FCSTD DOCUMENT  (FreeCAD 0.19R24267 +99 (Git))
Label: OTP20_Assembly
License: Creative Commons Attribution-NonCommercial-ShareAlike
LicenseURL: http://creativecommons.org/licenses/by-nc-sa/4.0/
objects: App::Link×6, App::DocumentObjectGroup×2, PartDesign::CoordinateSystem×1, App::FeaturePython×1, App::Part×1
note: 1 computed .brp shape members not serialized (recipe doc carries the construction recipe); baked Part::Feature solids carry a one-line shape summary decoded from their .brp
EXTERNAL_REF file=10_Case/OTP20_Case_Assembly.FCStd obj=LCS_Origin
EXTERNAL_REF file=10_Case/OTP20_Case_Assembly.FCStd obj=Model
EXTERNAL_REF file=30_PCB/OTP20_PCB_Assembly.FCStd obj=LCS_Origin
EXTERNAL_REF file=30_PCB/OTP20_PCB_Assembly.FCStd obj=Model
EXTERNAL_REF file=20_COTS/Battery_Pouch.FCStd obj=LCS_0
EXTERNAL_REF file=20_COTS/Battery_Pouch.FCStd obj=Battery_A5

FEATURE [App::DocumentObjectGroup] Parts
FEATURE [PartDesign::CoordinateSystem] LCS_Origin
  AttacherType = Attacher::AttachEngine3D
  MapMode = 2
  Support = -> [X_Axis]
FEATURE [App::DocumentObjectGroup] Constraints
FEATURE [App::FeaturePython] Variables  # WARN: FeaturePython — macro-defined, semantics opaque (R4)
FEATURE [App::Link] OTP20_Case_Assembly
  AssemblyType = Asm4EE
  AttachedBy = #LCS_Origin
  AttachedTo = Parent Assembly#LCS_Origin
  LinkedObject = -> <external 10_Case/OTP20_Case_Assembly.FCStd>#Model
  expr: Placement = LCS_Origin.Placement * AttachmentOffset * OTP20_Case_Assembly#LCS_Origin.Placement ^ -1
FEATURE [App::Link] OTP20_PCB_Assembly
  AssemblyType = Asm4EE
  AttachedBy = #LCS_Origin
  AttachedTo = Parent Assembly#LCS_Origin
  AttachmentOffset = pos=(-50,3,-1.6) rot=(0,0,1;0rad)
  LinkPlacement = pos=(-50,3,-1.6) rot=(0,0,1;0rad)
  LinkedObject = -> <external 30_PCB/OTP20_PCB_Assembly.FCStd>#Model
  Placement = pos=(-50,3,-1.6) rot=(0,0,1;0rad)
  expr: Placement = LCS_Origin.Placement * AttachmentOffset * OTP20_PCB_Assembly#LCS_Origin.Placement ^ -1
FEATURE [App::Link] Battery_Pouch_Cell_Galaxy_S6
  AttachedBy = #LCS_0
  AttachedTo = Parent Assembly#LCS_Origin
  AttachmentOffset = pos=(0,80,-8) rot=(0,0,1;0rad)
  LinkPlacement = pos=(0,80,-8) rot=(0,0,1;0rad)
  LinkedObject = -> <external 20_COTS/Battery_Pouch.FCStd>#Battery_A5
  Placement = pos=(0,80,-8) rot=(0,0,1;0rad)
  SolverId = Placement::ExpressionEngine
  expr: Placement = LCS_Origin.Placement * AttachmentOffset * Battery_Pouch#LCS_0.Placement ^ -1
FEATURE [App::Link] Battery_Pouch_Cell_Galaxy_S6001
  AttachedBy = #LCS_0
  AttachedTo = Battery_Pouch_Cell_Galaxy_S6#LCS_0
  AttachmentOffset = pos=(0,0,4) rot=(0,0,1;0rad)
  LinkPlacement = pos=(0,80,-4) rot=(0,0,1;0rad)
  LinkedObject = -> <external 20_COTS/Battery_Pouch.FCStd>#Battery_A5
  Placement = pos=(0,80,-4) rot=(0,0,1;0rad)
  SolverId = Placement::ExpressionEngine
  expr: Placement = Battery_Pouch_Cell_Galaxy_S6.Placement * Battery_Pouch#LCS_0.Placement * AttachmentOffset * Battery_Pouch#LCS_0.Placement ^ -1
FEATURE [App::Link] Battery_Pouch_Cell_Galaxy_S6002
  AttachedBy = #LCS_0
  AttachedTo = Battery_Pouch_Cell_Galaxy_S6001#LCS_0
  AttachmentOffset = pos=(0,0,4) rot=(0,0,1;0rad)
  LinkPlacement = pos=(0,80,0) rot=(0,0,1;0rad)
  LinkedObject = -> <external 20_COTS/Battery_Pouch.FCStd>#Battery_A5
  Placement = pos=(0,80,0) rot=(0,0,1;0rad)
  SolverId = Placement::ExpressionEngine
  expr: Placement = Battery_Pouch_Cell_Galaxy_S6001.Placement * Battery_Pouch#LCS_0.Placement * AttachmentOffset * Battery_Pouch#LCS_0.Placement ^ -1
FEATURE [App::Link] Battery_Pouch_Cell_Galaxy_S6003
  AttachedBy = #LCS_0
  AttachedTo = Battery_Pouch_Cell_Galaxy_S6002#LCS_0
  AttachmentOffset = pos=(0,0,4) rot=(0,0,1;0rad)
  LinkPlacement = pos=(0,80,4) rot=(0,0,1;0rad)
  LinkedObject = -> <external 20_COTS/Battery_Pouch.FCStd>#Battery_A5
  Placement = pos=(0,80,4) rot=(0,0,1;0rad)
  SolverId = Placement::ExpressionEngine
  expr: Placement = Battery_Pouch_Cell_Galaxy_S6002.Placement * Battery_Pouch#LCS_0.Placement * AttachmentOffset * Battery_Pouch#LCS_0.Placement ^ -1
FEATURE [App::Part] Model
  Configuration = 0
  Group = -> [LCS_Origin,Constraints,Variables,OTP20_Case_Assembly,OTP20_PCB_Assembly,Battery_Pouch_Cell_Galaxy_S6,Battery_Pouch_Cell_Galaxy_S6001,Battery_Pouch_Cell_Galaxy_S6002,Battery_Pouch_Cell_Galaxy_S6003]
  Origin = -> Origin
  Type = Assembly4 Model

RESOLVED EXTERNAL PARTS (link-assembly join: the EXTERNAL_REF files above that resolve inside this repo's crawl, each included once):
---- part 10_Case/OTP20_Case_Assembly.FCStd = doc fcstd_d594046b169b ----
FCSTD DOCUMENT  (FreeCAD 0.19R24267 +99 (Git))
Label: OTP20_Case_Assembly
License: Creative Commons Attribution-NonCommercial-ShareAlike
LicenseURL: http://creativecommons.org/licenses/by-nc-sa/4.0/
objects: Part::FeaturePython×8, App::Link×6, App::DocumentObjectGroup×3, PartDesign::CoordinateSystem×1, App::FeaturePython×1, App::Part×1
note: 9 computed .brp shape members not serialized (recipe doc carries the construction recipe); baked Part::Feature solids carry a one-line shape summary decoded from their .brp
EXTERNAL_REF file=KOH_Plate_Front.FCStd obj=LCS_0
EXTERNAL_REF file=KOH_Plate_Front.FCStd obj=Plate_Front
EXTERNAL_REF file=OTP20_Case_Bezel.FCStd obj=LCS_0
EXTERNAL_REF file=OTP20_Case_Bezel.FCStd obj=Bezel
EXTERNAL_REF file=KOH-2100.FCStd obj=LCS_KOH2100_CornerBottom
EXTERNAL_REF file=KOH_Plate_Front.FCStd obj=LCS_Plate_Front_CornerBottom
EXTERNAL_REF file=KOH-2100.FCStd obj=KOH_2100
EXTERNAL_REF file=KOH-0100.FCStd obj=LCS_0
EXTERNAL_REF file=KOH-0100.FCStd obj=KOH_0100
EXTERNAL_REF file=KOH_Plate_Back.FCStd obj=LCS_Plate_Back_CornerBottom
EXTERNAL_REF file=KOH_Plate_Back.FCStd obj=Plate_Back
EXTERNAL_REF file=KOH_Plate_Back.FCStd obj=LCS_0
EXTERNAL_REF file=KOH_Plate_Front.FCStd obj=LCS_Plate_Front_DisplayCenter
EXTERNAL_REF file=../20_COTS/Waveshare_OLED_0.91in.FCStd obj=LCS_OLEDDisplay_Center
EXTERNAL_REF file=../20_COTS/Waveshare_OLED_0.91in.FCStd obj=OLED_Display

FEATURE [App::DocumentObjectGroup] Parts
FEATURE [PartDesign::CoordinateSystem] LCS_Origin  label="LCS_Case_Origin"
  AttacherType = Attacher::AttachEngine3D
  MapMode = 2
  Support = -> [X_Axis]
FEATURE [App::DocumentObjectGroup] Constraints
FEATURE [App::FeaturePython] Variables  # WARN: FeaturePython — macro-defined, semantics opaque (R4)
FEATURE [App::Link] KOH_Plate_Front_Plate_Front
  AssemblyType = Asm4EE
  AttachedBy = #LCS_0
  AttachedTo = Parent Assembly#LCS_Origin
  LinkedObject = -> <external KOH_Plate_Front.FCStd>#Plate_Front
  expr: Placement = LCS_Origin.Placement * AttachmentOffset * KOH_Plate_Front#LCS_0.Placement ^ -1
FEATURE [App::Link] OTP20_Case_Bezel_Bezel
  AssemblyType = Asm4EE
  AttachedBy = #LCS_0
  AttachedTo = Parent Assembly#LCS_Origin
  AttachmentOffset = pos=(0,2,0) rot=(0,0,1;0rad)
  LinkPlacement = pos=(0,2,0) rot=(0,0,1;0rad)
  LinkedObject = -> <external OTP20_Case_Bezel.FCStd>#Bezel
  Placement = pos=(0,2,0) rot=(0,0,1;0rad)
  expr: Placement = LCS_Origin.Placement * AttachmentOffset * OTP20_Case_Bezel#LCS_0.Placement ^ -1
FEATURE [App::Link] KOH_2100_KOH_2100
  AssemblyType = Asm4EE
  AttachedBy = #LCS_KOH2100_CornerBottom
  AttachedTo = KOH_Plate_Front_Plate_Front#LCS_Plate_Front_CornerBottom
  AttachmentOffset = pos=(0,3,0) rot=(0,0,1;0rad)
  LinkPlacement = pos=(0,3,-14.35) rot=(0,0,1;0rad)
  LinkedObject = -> <external KOH-2100.FCStd>#KOH_2100
  Placement = pos=(0,3,-14.35) rot=(0,0,1;0rad)
  expr: Placement = KOH_Plate_Front_Plate_Front.Placement * KOH_Plate_Front#LCS_Plate_Front_CornerBottom.Placement * AttachmentOffset * KOH_2100#LCS_KOH2100_CornerBottom.Placement ^ -1
FEATURE [App::Link] KOH_0100_KOH_0100
  AssemblyType = Asm4EE
  AttachedBy = #LCS_0
  AttachedTo = KOH_2100_KOH_2100#LCS_KOH2100_CornerBottom
  AttachmentOffset = pos=(105,100,28.7) rot=(0,0,1;3.14159rad)
  LinkPlacement = pos=(52.5,103,14.35) rot=(0,0,1;3.14159rad)
  LinkedObject = -> <external KOH-0100.FCStd>#KOH_0100
  Placement = pos=(52.5,103,14.35) rot=(0,0,1;3.14159rad)
  SolverId = Placement::ExpressionEngine
  expr: Placement = KOH_2100_KOH_2100.Placement * KOH_2100#LCS_KOH2100_CornerBottom.Placement * AttachmentOffset * KOH_0100#LCS_0.Placement ^ -1
FEATURE [App::Link] KOH_Plate_Back_Plate_Back
  AssemblyType = Asm4EE
  AttachedBy = #LCS_Plate_Back_CornerBottom
  AttachedTo = KOH_Plate_Front_Plate_Front#LCS_Plate_Front_CornerBottom
  AttachmentOffset = pos=(0,105,0) rot=(0,0,1;0rad)
  LinkPlacement = pos=(0,105,1.95e-14) rot=(0,0,-1;3.14159rad)
  LinkedObject = -> <external KOH_Plate_Back.FCStd>#Plate_Back
  Placement = pos=(0,105,1.95e-14) rot=(0,0,-1;3.14159rad)
  SolverId = Placement::ExpressionEngine
  expr: Placement = KOH_Plate_Front_Plate_Front.Placement * KOH_Plate_Front#LCS_Plate_Front_CornerBottom.Placement * AttachmentOffset * KOH_Plate_Back#LCS_Plate_Back_CornerBottom.Placement ^ -1
FEATURE [Part::FeaturePython] Screw  label="M3x8-Screw"  # Fasteners workbench fastener (typed FeaturePython)
  AssemblyType = Asm4EE
  AttachedBy = Origin
  AttachedTo = KOH_Plate_Front_Plate_Front#LCS_0
  AttachmentOffset = pos=(46.5,0,10.85) rot=(0,0.707107,-0.707107;3.14159rad)
  Placement = pos=(46.5,0,10.85) rot=(0,0.707107,-0.707107;3.14159rad)
  diameter = 1
  invert = false
  length = 0
  lengthCustom = 8
  matchOuter = false
  offset = 0
  thread = false
  type = 17
  expr: Placement = KOH_Plate_Front_Plate_Front.Placement * KOH_Plate_Front#LCS_0.Placement * AttachmentOffset
FEATURE [Part::FeaturePython] Screw001  label="M3x8-Screw089"  # Fasteners workbench fastener (typed FeaturePython)
  AssemblyType = Asm4EE
  AttachedBy = Origin
  AttachedTo = KOH_Plate_Front_Plate_Front#LCS_0
  AttachmentOffset = pos=(46.5,0,-10.85) rot=(1,0,0;1.5708rad)
  Placement = pos=(46.5,0,-10.85) rot=(1,0,0;1.5708rad)
  diameter = 1
  invert = false
  length = 0
  lengthCustom = 8
  matchOuter = false
  offset = 0
  thread = false
  type = 17
  expr: Placement = KOH_Plate_Front_Plate_Front.Placement * KOH_Plate_Front#LCS_0.Placement * AttachmentOffset
FEATURE [Part::FeaturePython] Screw002  label="M3x8-Screw090"  # Fasteners workbench fastener (typed FeaturePython)
  AssemblyType = Asm4EE
  AttachedBy = Origin
  AttachedTo = KOH_Plate_Front_Plate_Front#LCS_0
  AttachmentOffset = pos=(-46.5,0,10.85) rot=(-1,0,0;4.71239rad)
  Placement = pos=(-46.5,0,10.85) rot=(1,0,0;1.5708rad)
  diameter = 1
  invert = false
  length = 0
  lengthCustom = 8
  matchOuter = false
  offset = 0
  thread = false
  type = 17
  expr: Placement = KOH_Plate_Front_Plate_Front.Placement * KOH_Plate_Front#LCS_0.Placement * AttachmentOffset
FEATURE [Part::FeaturePython] Screw003  label="M3x8-Screw091"  # Fasteners workbench fastener (typed FeaturePython)
  AssemblyType = Asm4EE
  AttachedBy = Origin
  AttachedTo = KOH_Plate_Front_Plate_Front#LCS_0
  AttachmentOffset = pos=(-46.5,0,-10.85) rot=(-0.57735,-0.57735,0.57735;4.18879rad)
  Placement = pos=(-46.5,0,-10.85) rot=(0.57735,0.57735,-0.57735;2.0944rad)
  diameter = 1
  invert = false
  length = 0
  lengthCustom = 8
  matchOuter = false
  offset = 0
  thread = false
  type = 17
  expr: Placement = KOH_Plate_Front_Plate_Front.Placement * KOH_Plate_Front#LCS_0.Placement * AttachmentOffset
FEATURE [Part::FeaturePython] Screw004  label="M3x8-Screw108"  # Fasteners workbench fastener (typed FeaturePython)
  AssemblyType = Asm4EE
  AttachedBy = Origin
  AttachedTo = KOH_Plate_Back_Plate_Back#LCS_0
  AttachmentOffset = pos=(46.5,0,10.85) rot=(-1,0,0;4.71239rad)
  Placement = pos=(-46.5,105,10.85) rot=(0,0.707107,0.707107;3.14159rad)
  diameter = 1
  invert = false
  length = 0
  lengthCustom = 8
  matchOuter = false
  offset = 0
  thread = false
  type = 17
  expr: Placement = KOH_Plate_Back_Plate_Back.Placement * KOH_Plate_Back#LCS_0.Placement * AttachmentOffset
FEATURE [Part::FeaturePython] Screw005  label="M3x8-Screw109"  # Fasteners workbench fastener (typed FeaturePython)
  AssemblyType = Asm4EE
  AttachedBy = Origin
  AttachedTo = KOH_Plate_Back_Plate_Back#LCS_0
  AttachmentOffset = pos=(46.5,0,-10.85) rot=(1,0,0;1.5708rad)
  Placement = pos=(-46.5,105,-10.85) rot=(0,0.707107,0.707107;3.14159rad)
  diameter = 1
  invert = false
  length = 0
  lengthCustom = 8
  matchOuter = false
  offset = 0
  thread = false
  type = 17
  expr: Placement = KOH_Plate_Back_Plate_Back.Placement * KOH_Plate_Back#LCS_0.Placement * AttachmentOffset
FEATURE [Part::FeaturePython] Screw006  label="M3x8-Screw110"  # Fasteners workbench fastener (typed FeaturePython)
  AssemblyType = Asm4EE
  AttachedBy = Origin
  AttachedTo = KOH_Plate_Back_Plate_Back#LCS_0
  AttachmentOffset = pos=(-46.5,0,10.85) rot=(1,0,0;1.5708rad)
  Placement = pos=(46.5,105,10.85) rot=(0,0.707107,0.707107;3.14159rad)
  diameter = 1
  invert = false
  length = 0
  lengthCustom = 8
  matchOuter = false
  offset = 0
  thread = false
  type = 17
  expr: Placement = KOH_Plate_Back_Plate_Back.Placement * KOH_Plate_Back#LCS_0.Placement * AttachmentOffset
FEATURE [Part::FeaturePython] Screw007  label="M3x8-Screw111"  # Fasteners workbench fastener (typed FeaturePython)
  AssemblyType = Asm4EE
  AttachedBy = Origin
  AttachedTo = KOH_Plate_Back_Plate_Back#LCS_0
  AttachmentOffset = pos=(-46.5,0,-10.85) rot=(-1,0,0;4.71239rad)
  Placement = pos=(46.5,105,-10.85) rot=(0,0.707107,0.707107;3.14159rad)
  diameter = 1
  invert = false
  length = 0
  lengthCustom = 8
  matchOuter = false
  offset = 0
  thread = false
  type = 17
  expr: Placement = KOH_Plate_Back_Plate_Back.Placement * KOH_Plate_Back#LCS_0.Placement * AttachmentOffset
FEATURE [App::DocumentObjectGroup] Group  label="Screws"
  Group = -> [Screw,Screw001,Screw002,Screw003,Screw004,Screw005,Screw006,Screw007]
FEATURE [App::Link] Waveshare_OLED_0_91in_OLED_Display
  AssemblyType = Asm4EE
  AttachedBy = #LCS_OLEDDisplay_Center
  AttachedTo = KOH_Plate_Front_Plate_Front#LCS_Plate_Front_DisplayCenter
  AttachmentOffset = pos=(0,-0.09,-2) rot=(0,0,1;3.14159rad)
  LinkPlacement = pos=(36.19,5.3,9.55) rot=(0,-1,0;3.14159rad)
  LinkedObject = -> <external ../20_COTS/Waveshare_OLED_0.91in.FCStd>#OLED_Display
  Placement = pos=(36.19,5.3,9.55) rot=(0,-1,0;3.14159rad)
  expr: Placement = KOH_Plate_Front_Plate_Front.Placement * KOH_Plate_Front#LCS_Plate_Front_DisplayCenter.Placement * AttachmentOffset * Waveshare_OLED_0_91in#LCS_OLEDDisplay_Center.Placement ^ -1
FEATURE [App::Part] Model
  Configuration = 0
  Group = -> [LCS_Origin,Constraints,Variables,KOH_Plate_Front_Plate_Front,OTP20_Case_Bezel_Bezel,KOH_2100_KOH_2100,KOH_0100_KOH_0100,KOH_Plate_Back_Plate_Back,Group,Screw,Screw001,Screw002,Screw003,Screw004,Screw005,Screw006,Screw007,Waveshare_OLED_0_91in_OLED_Display]
  Origin = -> Origin
  Type = Assembly4 Model
---- part 20_COTS/Battery_Pouch.FCStd = doc fcstd_cdebb19cccf6 ----
FCSTD DOCUMENT  (FreeCAD 0.19R24267 +99 (Git))
Label: Battery_Pouch
License: Creative Commons Attribution-NonCommercial-ShareAlike
LicenseURL: http://creativecommons.org/licenses/by-nc-sa/4.0/
objects: PartDesign::CoordinateSystem×2, Sketcher::SketchObject×1, PartDesign::Pad×1, PartDesign::Fillet×1, PartDesign::Body×1, App::Part×1
note: 8 computed .brp shape members not serialized (recipe doc carries the construction recipe); baked Part::Feature solids carry a one-line shape summary decoded from their .brp

FEATURE [PartDesign::CoordinateSystem] LCS_0  label="LCS_Origin"
  AttacherType = Attacher::AttachEngine3D
  MapMode = 2
  Support = -> [X_Axis]
FEATURE [PartDesign::CoordinateSystem] LCS_0001
  AttacherType = Attacher::AttachEngine3D
  MapMode = 2
  Support = -> [X_Axis001]
FEATURE [Sketcher::SketchObject] Sketch
  FullyConstrained = true
  MapMode = 5
  Placement = pos=(0,0,0) rot=(0.57735,0.57735,0.57735;2.0944rad)
  Support = -> [YZ_Plane001]
  sketch-geometry (4):
    g0: LineSegment StartX=-21.35 StartY=0 StartZ=0 EndX=21.35 EndY=0 EndZ=0
    g1: LineSegment StartX=-21.35 StartY=4 StartZ=0 EndX=21.35 EndY=4 EndZ=0
    g2: LineSegment StartX=21.35 StartY=4 StartZ=0 EndX=21.35 EndY=0 EndZ=0
    g3: LineSegment StartX=-21.35 StartY=4 StartZ=0 EndX=-21.35 EndY=0 EndZ=0
  constraints (11):
    c: Horizontal(g0)
    c: Coincident(g2,g1)
    c: Coincident(g2,g0)
    c: Coincident(g3,g1)
    c: Coincident(g3,g0)
    c: Vertical(g3)
    c: Vertical(g2)
    c: Symmetric(g1,g1,g-2)
    c: Distance(g1) = 42.7
    c: DistanceY(g1) = 4
    c: PointOnObject(g-1,g0)
FEATURE [PartDesign::Pad] Pad
  Direction = (1,1,1)
  Length = 93.4
  Length2 = 100
  Midplane = true
  Placement = pos=(0,0,0) rot=(0.57735,0.57735,0.57735;2.0944rad)
  Profile = -> Sketch
  Refine = true
  Type = 0
FEATURE [PartDesign::Fillet] Fillet
  Base = -> Pad [Edge1,Edge2,Edge5,Edge8]
  BaseFeature = -> Pad
  Placement = pos=(0,0,0) rot=(0.57735,0.57735,0.57735;2.0944rad)
  Radius = 1
  Refine = true
  SupportTransform = false
FEATURE [PartDesign::Body] Main
  Group = -> [LCS_0001,Sketch,Pad,Fillet]
  Origin = -> Origin001
  Tip = -> Fillet
FEATURE [App::Part] Battery_A5  label="Cell_Galaxy_S6"
  Group = -> [LCS_0,Main]
  Origin = -> Origin
---- part 30_PCB/OTP20_PCB_Assembly.FCStd = doc fcstd_e5338bbabf42 ----
FCSTD DOCUMENT  (FreeCAD 0.19R24267 +99 (Git))
Label: OTP20_PCB_Assembly
License: Creative Commons Attribution-NonCommercial-ShareAlike
LicenseURL: http://creativecommons.org/licenses/by-nc-sa/4.0/
objects: App::Link×6, App::DocumentObjectGroup×2, PartDesign::CoordinateSystem×1, App::FeaturePython×1, App::Part×1
note: 1 computed .brp shape members not serialized (recipe doc carries the construction recipe); baked Part::Feature solids carry a one-line shape summary decoded from their .brp
EXTERNAL_REF file=PCB_Outline.FCStd obj=LCS_0
EXTERNAL_REF file=PCB_Outline.FCStd obj=PCB_Board
EXTERNAL_REF file=../20_COTS/Lightpipe_Mentor_1296-2012.FCStd obj=LCS_0
EXTERNAL_REF file=../20_COTS/Lightpipe_Mentor_1296-2012.FCStd obj=Lightpipe
EXTERNAL_REF file=../20_COTS/USB_A_Connector_Wuerth.FCStd obj=USB_A_Connector
EXTERNAL_REF file=../20_COTS/USB_A_Connector_Wuerth.FCStd obj=LCS_0
EXTERNAL_REF file=../20_COTS/USB_C_Connector_Wuerth.FCStd obj=USB_C_Connector
EXTERNAL_REF file=Main_PCB.FCStd obj=LCS_0
EXTERNAL_REF file=Main_PCB.FCStd obj=Main_PCB

FEATURE [App::DocumentObjectGroup] Parts
FEATURE [PartDesign::CoordinateSystem] LCS_Origin  label="LCS_PCB"
  AttacherType = Attacher::AttachEngine3D
  MapMode = 2
  Support = -> [X_Axis]
FEATURE [App::DocumentObjectGroup] Constraints
FEATURE [App::FeaturePython] Variables  # WARN: FeaturePython — macro-defined, semantics opaque (R4)
  Connector_Inserted = 20
FEATURE [App::Link] PCB_Outline_PCB_Board
  AssemblyType = Asm4EE
  AttachedBy = #LCS_0
  AttachedTo = Parent Assembly#LCS_Origin
  LinkedObject = -> <external PCB_Outline.FCStd>#PCB_Board
  expr: Placement = LCS_Origin.Placement * AttachmentOffset * PCB_Outline#LCS_0.Placement ^ -1
FEATURE [App::Link] Lightpipe_Mentor_1296_2012_Lightpipe
  AssemblyType = Asm4EE
  AttachedBy = #LCS_0
  AttachedTo = PCB_Outline_PCB_Board#LCS_0
  AttachmentOffset = pos=(88,0,2.54) rot=(0,0,1;4.71239rad)
  LinkPlacement = pos=(88,0,2.54) rot=(0,0,1;4.71239rad)
  LinkedObject = -> <external ../20_COTS/Lightpipe_Mentor_1296-2012.FCStd>#Lightpipe
  Placement = pos=(88,0,2.54) rot=(0,0,1;4.71239rad)
  expr: Placement = PCB_Outline_PCB_Board.Placement * PCB_Outline#LCS_0.Placement * AttachmentOffset * Lightpipe_Mentor_1296_2012#LCS_0.Placement ^ -1
FEATURE [App::Link] USB_A_Connector_Wuerth_USB_A_Connector
  AssemblyType = Asm4EE
  AttachedBy = #LCS_0
  AttachedTo = Parent Assembly#LCS_Origin
  AttachmentOffset = pos=(42,-4,4.05) rot=(0,0,1;3.14159rad)
  LinkPlacement = pos=(42,-24,4.05) rot=(0,0,1;3.14159rad)
  LinkedObject = -> <external ../20_COTS/USB_A_Connector_Wuerth.FCStd>#USB_A_Connector
  Placement = pos=(42,-24,4.05) rot=(0,0,1;3.14159rad)
  expr: .Placement.Base.y = -4mm - Variables.Connector_Inserted * 1mm
FEATURE [App::Link] USB_A_Connector_Wuerth_USB_A_Connector001
  AssemblyType = Asm4EE
  AttachedBy = #LCS_0
  AttachedTo = USB_A_Connector_Wuerth_USB_A_Connector#LCS_0
  AttachmentOffset = pos=(18,0,0) rot=(0,0,1;0rad)
  LinkPlacement = pos=(24,-24,4.05) rot=(0,0,1;3.14159rad)
  LinkedObject = -> <external ../20_COTS/USB_A_Connector_Wuerth.FCStd>#USB_A_Connector
  Placement = pos=(24,-24,4.05) rot=(0,0,1;3.14159rad)
  expr: Placement = USB_A_Connector_Wuerth_USB_A_Connector.Placement * USB_A_Connector_Wuerth#LCS_0.Placement * AttachmentOffset * USB_A_Connector_Wuerth#LCS_0.Placement ^ -1
FEATURE [App::Link] USB_C_Connector_Wuerth_USB_C_Connector
  AssemblyType = Asm4EE
  AttachedBy = #LCS_USB_C_CenterCase
  AttachedTo = PCB_Outline_PCB_Board#LCS_0
  AttachmentOffset = pos=(7,-1,1.5) rot=(1,0,0;1.5708rad)
  LinkPlacement = pos=(7,-17,1.5) rot=(0,-0.707107,-0.707107;3.14159rad)
  LinkedObject = -> <external ../20_COTS/USB_C_Connector_Wuerth.FCStd>#USB_C_Connector
  Placement = pos=(7,-17,1.5) rot=(0,-0.707107,-0.707107;3.14159rad)
  expr: .Placement.Base.y = 3mm - Variables.Connector_Inserted * 1mm
FEATURE [App::Link] Main_PCB_Main_PCB
  AssemblyType = Asm4EE
  AttachedBy = #LCS_0
  AttachedTo = PCB_Outline_PCB_Board#LCS_0
  LinkedObject = -> <external Main_PCB.FCStd>#Main_PCB
  expr: Placement = PCB_Outline_PCB_Board.Placement * PCB_Outline#LCS_0.Placement * AttachmentOffset * Main_PCB#LCS_0.Placement ^ -1
FEATURE [App::Part] Model
  Configuration = 0
  Group = -> [LCS_Origin,Constraints,Variables,PCB_Outline_PCB_Board,Lightpipe_Mentor_1296_2012_Lightpipe,USB_A_Connector_Wuerth_USB_A_Connector,USB_A_Connector_Wuerth_USB_A_Connector001,USB_C_Connector_Wuerth_USB_C_Connector,Main_PCB_Main_PCB]
  Origin = -> Origin
  Type = Assembly4 Model
